# Revit family: Superstreet 340
name_source: partatom
category: Осветительные приборы
revit_build: Autodesk Revit 2017 (Build: 20160225_1515(x64)
units: mm (PartAtom-declared; Revit-internal decimal feet)

## family parameters
Всегда вертикально = Да
Источник света = Да
На основе рабочей плоскости = Нет
Общий = Нет
При загрузке вырезать с полостями = Нет
Размер круглого соединителя = Использовать диаметр
Тип детали = Нормальный
Точка расчета площади = Нет

## types (10) — shared parameters
Видимая форма излучения при визуализации = Нет
Изготовитель = LEDEL
Излучение по длине прямоугольника = 560 мм
Излучение по ширине прямоугольника = 95 мм
Классификация нагрузок = Освещение
Комментарии к типоразмеру = Уличные
Полная установленная мощность = 310 В·А
Светофильтр = 16777215
Смещение цветовой температуры при затухании лампы = <Нет>
Угол наклона = 90.00°

## per-type parameters (varying)
| type | Артикул | Файл фотометрической сетки |
| Superstreet 340 4.0К Ш7 | 306118 | Superstreet 340-310-LLI7-4.0K-05.ies |
| Superstreet 340 4.0К Ш8 | 306117 | Superstreet 340-310-LLI8-4.0K-01.ies |
| Superstreet 340 4.0К Ш13 | 306116 | Superstreet 340-310-LLI13-4.0K-01.ies |
| Superstreet 340 4.0К Ш22 |  | Superstreet 340-310-LLI22-4.0К-01.ies |
| Superstreet 340 4.0К Ш23 |  | Superstreet 340-310-LLI23-4.0К-01.ies |
| Superstreet 340 5.0К Ш23 |  | Superstreet 340-310-LLI23-5.0К-01.ies |
| Superstreet 340 5.0К Ш13 | 306110 | Superstreet 340-310-LLI13-5.0К-01.ies |
| Superstreet 340 5.0К Ш7 | 306119 | Superstreet 340-310-LLI7-5.0K-05.ies |
| Superstreet 340 5.0К Ш8 | 306115 | Superstreet 340-310-LLI8-5.0K-01.ies |
| Superstreet 340 5.0К Ш22 |  | Superstreet 340-310-LLI22-5.0К-01.ies |
